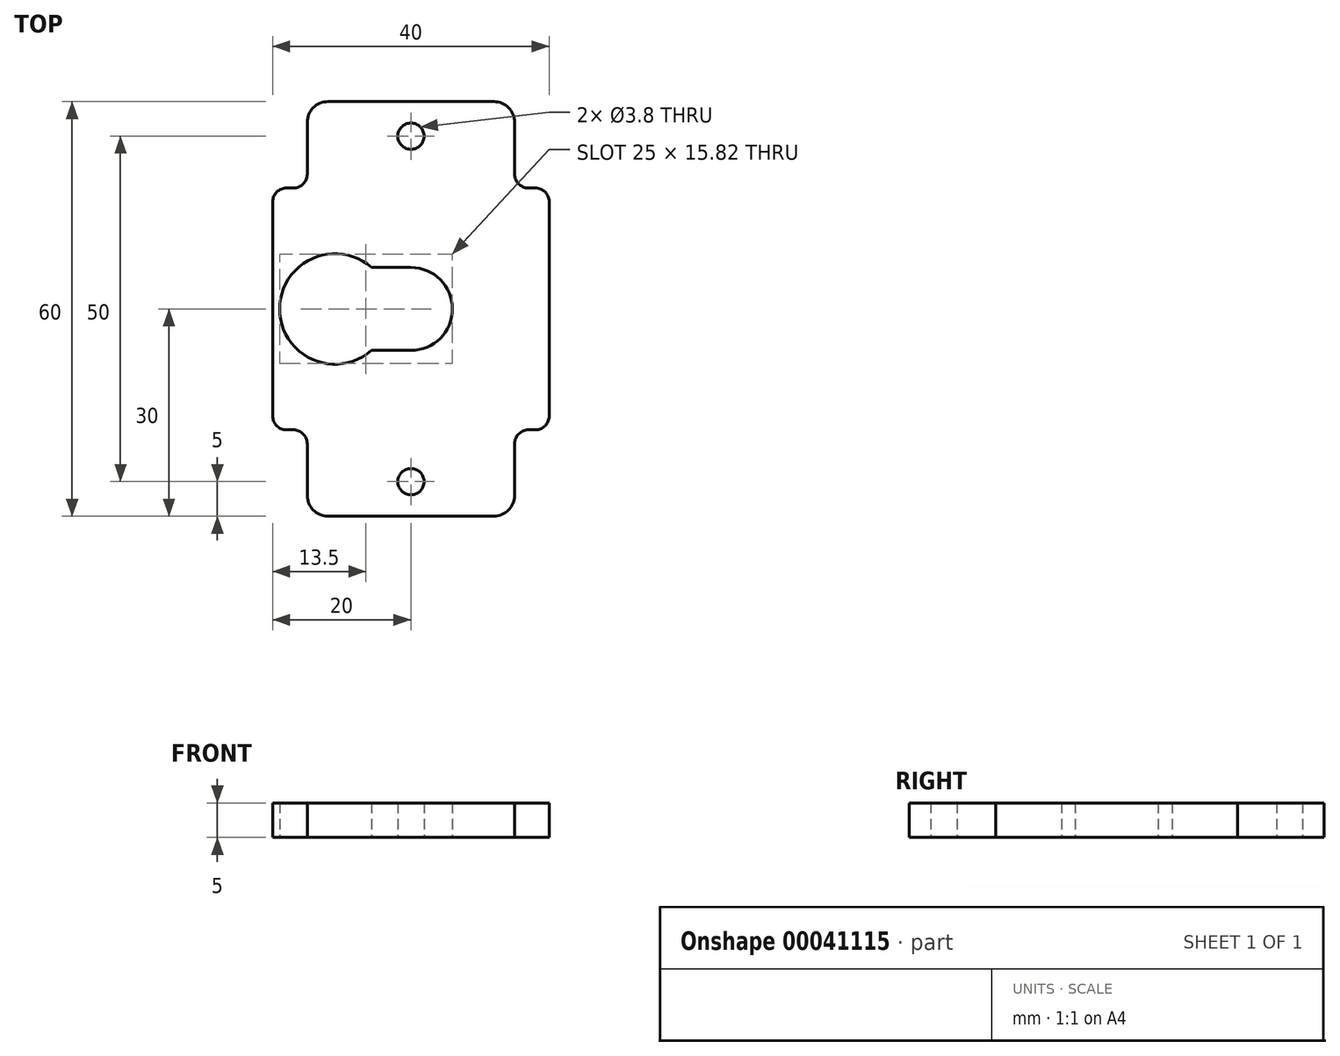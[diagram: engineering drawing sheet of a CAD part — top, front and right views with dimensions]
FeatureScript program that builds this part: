
annotation { "Feature Type Name" : "Feature", "Feature Type Description" : "" }
export const myFeature = defineFeature(function(context is Context, id is Id, definition is map)
    precondition{}
    {
        {
            var Q0;
            Q0=qCreatedBy(makeId("Top.planeOp"),FACE);
            var sketch = newSketch(context, id + "F0", { "sketchPlane" : qUnion([Q0])});
            skLineSegment(sketch, "E0.rect.bottom", {"start": v(12, -30) * mm, "end": v(-12, -30) * mm});
            skLineSegment(sketch, "E0.rect.top", {"start": v(12, 30) * mm, "end": v(-12, 30) * mm});
            skLineSegment(sketch, "E0.rect.left", {"start": v(15, -27) * mm, "end": v(15, -19.5) * mm});
            skLineSegment(sketch, "E0.rect.right", {"start": v(-15, -27) * mm, "end": v(-15, -19.5) * mm});
            skPoint(sketch, "E0.rect.middle", {"position": v(0, 0) * mm});
            skPoint(sketch, "E1.visualSharp", {"position": v(-15, 30) * mm});
            skArc(sketch, "E1.filletArc", {"start": v(-12, 30) * mm, "mid": v(-14.12, 29.12) * mm, "end": v(-15, 27) * mm});
            skPoint(sketch, "E2.visualSharp", {"position": v(15, 30) * mm});
            skArc(sketch, "E2.filletArc", {"start": v(15, 27) * mm, "mid": v(14.12, 29.12) * mm, "end": v(12, 30) * mm});
            skPoint(sketch, "E3.visualSharp", {"position": v(15, -30) * mm});
            skArc(sketch, "E3.filletArc", {"start": v(12, -30) * mm, "mid": v(14.12, -29.12) * mm, "end": v(15, -27) * mm});
            skPoint(sketch, "E4.visualSharp", {"position": v(-15, -30) * mm});
            skArc(sketch, "E4.filletArc", {"start": v(-15, -27) * mm, "mid": v(-14.12, -29.12) * mm, "end": v(-12, -30) * mm});
            skLineSegment(sketch, "E5.rect.bottom", {"start": v(18, 17.5) * mm, "end": v(17, 17.5) * mm});
            skLineSegment(sketch, "E5.rect.top", {"start": v(18, -17.5) * mm, "end": v(17, -17.5) * mm});
            skLineSegment(sketch, "E5.rect.left", {"start": v(20, 15.5) * mm, "end": v(20, -15.5) * mm});
            skLineSegment(sketch, "E5.rect.right", {"start": v(-20, 15.5) * mm, "end": v(-20, -15.5) * mm});
            skLineSegment(sketch, "E6.trimOffspring", {"start": v(-17, 17.5) * mm, "end": v(-18, 17.5) * mm});
            skLineSegment(sketch, "E7.trimOffspring", {"start": v(-15, 19.5) * mm, "end": v(-15, 27) * mm});
            skLineSegment(sketch, "E8.trimOffspring", {"start": v(15, 19.5) * mm, "end": v(15, 27) * mm});
            skLineSegment(sketch, "E9.trimOffspring", {"start": v(-17, -17.5) * mm, "end": v(-18, -17.5) * mm});
            skPoint(sketch, "E10.visualSharp", {"position": v(-15, 17.5) * mm});
            skArc(sketch, "E10.filletArc", {"start": v(-17, 17.5) * mm, "mid": v(-15.59, 18.09) * mm, "end": v(-15, 19.5) * mm});
            skPoint(sketch, "E11.visualSharp", {"position": v(-20, 17.5) * mm});
            skArc(sketch, "E11.filletArc", {"start": v(-18, 17.5) * mm, "mid": v(-19.41, 16.91) * mm, "end": v(-20, 15.5) * mm});
            skPoint(sketch, "E12.visualSharp", {"position": v(-20, -17.5) * mm});
            skArc(sketch, "E12.filletArc", {"start": v(-20, -15.5) * mm, "mid": v(-19.41, -16.91) * mm, "end": v(-18, -17.5) * mm});
            skPoint(sketch, "E13.visualSharp", {"position": v(-15, -17.5) * mm});
            skArc(sketch, "E13.filletArc", {"start": v(-15, -19.5) * mm, "mid": v(-15.59, -18.09) * mm, "end": v(-17, -17.5) * mm});
            skPoint(sketch, "E14.visualSharp", {"position": v(15, -17.5) * mm});
            skArc(sketch, "E14.filletArc", {"start": v(17, -17.5) * mm, "mid": v(15.59, -18.09) * mm, "end": v(15, -19.5) * mm});
            skPoint(sketch, "E15.visualSharp", {"position": v(20, -17.5) * mm});
            skArc(sketch, "E15.filletArc", {"start": v(18, -17.5) * mm, "mid": v(19.41, -16.91) * mm, "end": v(20, -15.5) * mm});
            skPoint(sketch, "E16.visualSharp", {"position": v(20, 17.5) * mm});
            skArc(sketch, "E16.filletArc", {"start": v(20, 15.5) * mm, "mid": v(19.41, 16.91) * mm, "end": v(18, 17.5) * mm});
            skPoint(sketch, "E17.visualSharp", {"position": v(15, 17.5) * mm});
            skArc(sketch, "E17.filletArc", {"start": v(15, 19.5) * mm, "mid": v(15.59, 18.09) * mm, "end": v(17, 17.5) * mm});
            skArc(sketch, "E18", {"start": v(0, -6) * mm, "mid": v(6, 0) * mm, "end": v(0, 6) * mm});
            skArc(sketch, "E19", {"start": v(-5.7, 6) * mm, "mid": v(-19, 0) * mm, "end": v(-5.7, -6) * mm});
            skLineSegment(sketch, "E20.bottom", {"start": v(0, 6) * mm, "end": v(-5.7, 6) * mm});
            skLineSegment(sketch, "E21.bottom", {"start": v(0, -6) * mm, "end": v(-5.7, -6) * mm});
            skCircle(sketch, "E22", {"center": v(0, 25) * mm, "radius": 1.9 * mm});
            skCircle(sketch, "E23", {"center": v(0, -25) * mm, "radius": 1.9 * mm});
            skSolve(sketch);
        }
        {
            var Q0;
            Q0 = qSketchRegion(id + "F0", true);
            extrude(context, id + "F1", {"entities" : qUnion([Q0]), "depth" : 5 * mm});
        }
    });
